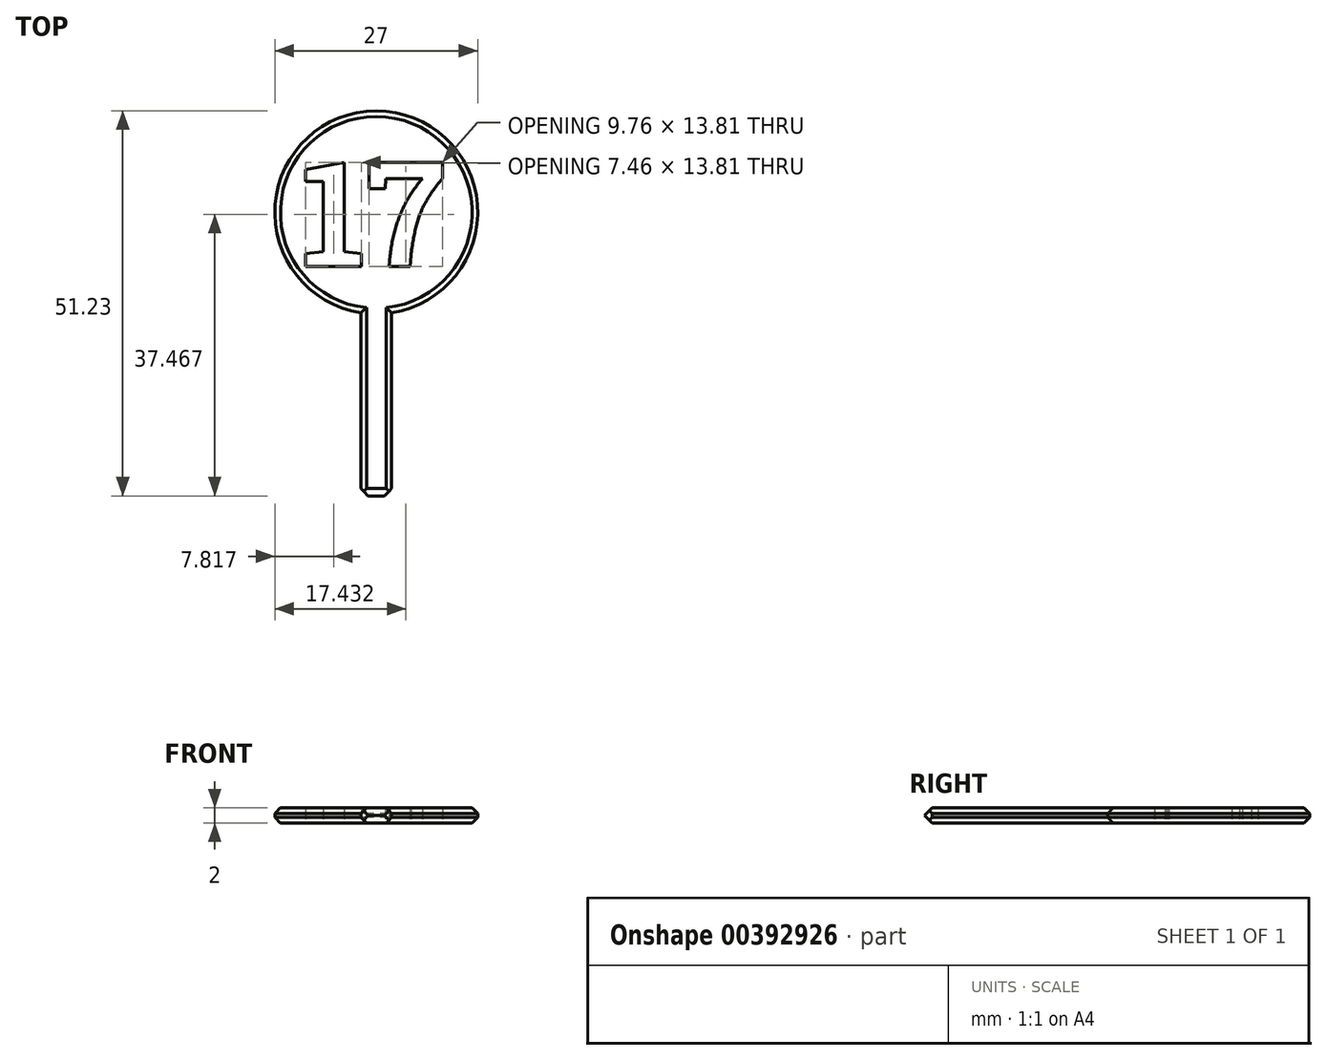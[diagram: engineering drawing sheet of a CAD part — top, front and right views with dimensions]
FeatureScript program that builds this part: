
annotation { "Feature Type Name" : "Feature", "Feature Type Description" : "" }
export const myFeature = defineFeature(function(context is Context, id is Id, definition is map)
    precondition{}
    {
        {
            var Q0;
            Q0=qCreatedBy(makeId("Top.planeOp"),FACE);
            var sketch = newSketch(context, id + "F0", { "sketchPlane" : qUnion([Q0])});
            skLineSegment(sketch, "E0", {"start": v(0, 12.1) * mm, "end": v(0, -11.88) * mm, "construction": true});
            skLineSegment(sketch, "E1", {"start": v(-10.82, 0) * mm, "end": v(11.65, 0) * mm, "construction": true});
            skText(sketch, "E2", { "text": "17", "fontName": "RobotoSlab-Bold.ttf"});
            skCircle(sketch, "E3", {"center": v(0, 0) * mm, "radius": 13.5 * mm});
            skLineSegment(sketch, "E4", {"start": v(0, -11.88) * mm, "end": v(0, -19.61) * mm, "construction": true});
            skLineSegment(sketch, "E5", {"start": v(-2.05, -13.34) * mm, "end": v(-2.05, -37.73) * mm});
            skLineSegment(sketch, "E6.MirrorCS", {"start": v(2.05, -13.34) * mm, "end": v(2.05, -37.73) * mm});
            skLineSegment(sketch, "E7", {"start": v(-2.05, -37.73) * mm, "end": v(2.05, -37.73) * mm});
            const initialGuessF0  = {"E2": [-0.01, -0.00717, 1, 0, 0.01399]};
            skSetInitialGuess(sketch, initialGuessF0);
            skSolve(sketch);
        }
        {
            var Q0;
            Q0 = qSketchRegion(id + "F0", true);
            extrude(context, id + "F1", {"entities" : qUnion([Q0]), "depth" : 2 * mm});
        }
        {
            var Q0;
            Q0=makeQuery(id+"F1.opExtrude","CAP_EDGE",EDGE,{"disambiguationData":[OSD([sQuery(id+"F0.wireOp",EDGE,"E7")])],"isStart":false});
            var Q1;
            Q1=makeQuery(id+"F1.opExtrude","CAP_EDGE",EDGE,{"disambiguationData":[OSD([sQuery(id+"F0.wireOp",EDGE,"E7")])],"isStart":true});
            var Q2;
            Q2=makeQuery(id+"F1.opExtrude","SWEPT_EDGE",EDGE,{"disambiguationData":[OSD([sQuery(id+"F0.wireOp",EDGE,"E6.MirrorCS"),sQuery(id+"F0.wireOp",EDGE,"E7")])]});
            var Q3;
            Q3=makeQuery(id+"F1.opExtrude","SWEPT_EDGE",EDGE,{"disambiguationData":[OSD([sQuery(id+"F0.wireOp",EDGE,"E5"),sQuery(id+"F0.wireOp",EDGE,"E7")])]});
            chamfer(context, id + "F2", {"entities" : qUnion([Q0, Q1, Q2, Q3]), "width" : 1 * mm, "tangentPropagation" : true});
        }
        {
            var Q0;
            Q0=makeQuery(id+"F1.opExtrude","CAP_EDGE",EDGE,{"disambiguationData":[OSD([sQuery(id+"F0.wireOp",EDGE,"E3")])],"isStart":false});
            var Q1;
            Q1=makeQuery(id+"F1.opExtrude","CAP_EDGE",EDGE,{"disambiguationData":[OSD([sQuery(id+"F0.wireOp",EDGE,"E5")])],"isStart":false});
            var Q2;
            Q2=makeQuery(id+"F1.opExtrude","CAP_EDGE",EDGE,{"disambiguationData":[OSD([sQuery(id+"F0.wireOp",EDGE,"E6.MirrorCS")])],"isStart":false});
            var Q3;
            Q3=makeQuery(id+"F1.opExtrude","CAP_EDGE",EDGE,{"disambiguationData":[OSD([sQuery(id+"F0.wireOp",EDGE,"E3")])],"isStart":true});
            var Q4;
            Q4=makeQuery(id+"F1.opExtrude","CAP_EDGE",EDGE,{"disambiguationData":[OSD([sQuery(id+"F0.wireOp",EDGE,"E5")])],"isStart":true});
            var Q5;
            Q5=makeQuery(id+"F1.opExtrude","CAP_EDGE",EDGE,{"disambiguationData":[OSD([sQuery(id+"F0.wireOp",EDGE,"E6.MirrorCS")])],"isStart":true});
            chamfer(context, id + "F3", {"entities" : qUnion([Q0, Q1, Q2, Q3, Q4, Q5]), "width" : .75 * mm, "tangentPropagation" : true});
        }
    });
